# Revit family: LAMP_KOMBIC 200 RD TW
name_source: partatom
category: Luminarias
revit_build: Autodesk Revit 2018 (Build: 20190510_1515(x64)
units: mm (PartAtom-declared; Revit-internal decimal feet)

## family parameters
Anfitrión = Techo
Compartido = No
Corte con vacíos al cargar = No
Cota de conector redondo = Diámetro de uso
Número OmniClass = 23.80.70.11
Origen de luz = Sí
Punto de cálculo de habitación = No
Siempre vertical = Sí
Tipo de pieza = Normal
Título OmniClass = Luminaries for Internal Lighting

## types (4) — shared parameters
Altura central = 62 mm  [stored 0.203412 ft]
Altura exterior = 106 mm  [stored 0.347769 ft]
CCT = 2700-6500
CRI = 90
Cambio de temperatura de color de luz atenuada = <Ninguno>
Comentarios de tipo = Availability of switching between accessories through visibility parameters when placed in a project.
Diam. exterior cuerpo = 167 mm  [stored 0.5479 ft]
Diam. inferior cuerpo = 220 mm  [stored 0.721785 ft]
Diam. inferior interior = 188 mm  [stored 0.616798 ft]
Diameter = 220 mm  [stored 0.721785 ft]
Fabricante = LAMP
Filtro de color = 16777215
Finish = RAL9010
Gear = Electronic
Height = 106 mm  [stored 0.347769 ft]
IEE = A+
Installation instructions = https://www.lamp.es
Insulation class = II
Last update = 24/02/2022
Lámpara = MID-POWER LED
MacAdam = 3
Manufacturer URL = http://www.lamp.es
Manufacturer country = Spain
Manufacturer name = LAMP
Material Armazón BL = LAMP_PC Armazón Kombic BL
Material Armazón GR = LAMP_PC Armazón Kombic GR
Material Difusor = LAMP_PMMA Difusor Kombic
Material Disipador = LAMP_Aluminio Disipador Kombic
Model explanation = Availability of switching between accessories through visibility parameters when placed in a project.
Photobiological risk = Group 0
Product URL = https://www.lamp.es
Product datasheet = http://www.lamp.es
Protection rating = IP44
Recessed diameter = 209 mm  [stored 0.685696 ft]
Type = MID POWER NICHIA
Weight = 0.98 kg
Ángulo de inclinación = 90.00°

## per-type parameters (varying)
| type | Archivo de red fotométrica | Descripción | Efficacy | LED Lifetime | Material Reflector | Modelo | Plum | Power | Power Supply | Product code |
| 1355LM 2700-6500 MATT BLANCO | K31RD2040OP9TWDMW_4000K.IES | KOMBIC 200 RD 2000 IP44 TW OPAL DA MA/WH | 87 lm/W | 50.000 L90 B10 | LAMP_PC Reflector Kombic Metalizado Mate | K31RD2040OP9TWDMW | 16 W | 12 W | 220-240V 50-60Hz | K31RD2040OP9TWDMW |
| 1506LM 2700-6500 BRIGHT BLANCO | K31RD2040OP9TWDRW_4000K.IES | KOMBIC 200 RD 2000 IP44 TW OPAL DA BR/WH | 97 lm/W | 50.000 L90 B10 | LAMP_PC Reflector Kombic Metalizado Brillante | K31RD2040OP9TWDRW | 16 W | 12 W | 220-240V 50/60Hz | K31RD2040OP9TWDRW |
| 1989LM 2700-6500 MATT BLANCO | K31RD3040OP9TWDMW_4000K.IES | KOMBIC 200 RD 3000 IP44 TW OPAL DA MA/WH | 89 lm/W | 50.000 L80 B10 | LAMP_PC Reflector Kombic Metalizado Mate | K31RD3040OP9TWDMW | 22 W | 18 W | 220-240V 50-60Hz | K31RD3040OP9TWDMW |
| 2161LM 2700-6500 BRIGHT BLANCO | K31RD3040OP9TWDRW_4000k.IES | KOMBIC 200 RD 3000 IP44 TW OPAL DA BR/WH | 97 lm/W | 50.000 L80 B10 | LAMP_PC Reflector Kombic Metalizado Brillante | K31RD3040OP9TWDRW | 22 W | 18 W | 220-240V 50-60Hz | K31RD3040OP9TWDRW |

note: [stored X ft] marks values corroborated as IEEE doubles in the binary element streams (Revit-internal decimal feet)

## geometry (parser evidence)
native form markers: Blend x2
no freeform markers — native parametric forms only
